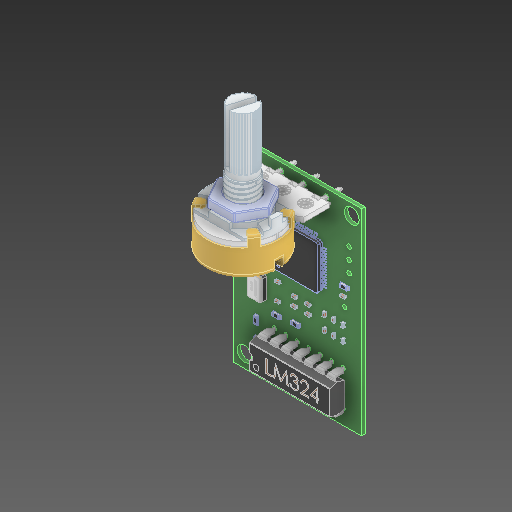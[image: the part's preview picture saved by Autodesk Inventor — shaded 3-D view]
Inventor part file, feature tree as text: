
AUTODESK INVENTOR PART (.ipt)
format: ipt  version: 2020 (Build 240168000, 168)  size: 4,296,704 bytes
history: native  units: in
note: dims shown in document units (in); Inventor stores cm internally (conversion verified against a paired STEP export)
features: other x95, extrude x1
ambient origin geometry x8: Origin, YZ Plane, XZ Plane, XY Plane, X Axis, Y Axis, Z Axis, Center Point
bodies: Solid1 (feature_tree), Solid2 (feature_tree), Solid3 (feature_tree), Solid4 (feature_tree), Solid5 (feature_tree), Solid6 (feature_tree), Solid7 (feature_tree), Solid8 (feature_tree), Solid9 (feature_tree), Solid10 (feature_tree), Solid11 (feature_tree), Solid12 (feature_tree), Solid13 (feature_tree), Solid14 (feature_tree), Solid15 (feature_tree), Solid16 (feature_tree), Solid17 (feature_tree), Solid18 (feature_tree), Solid19 (feature_tree), Solid20 (feature_tree), Solid21 (feature_tree), Solid22 (feature_tree), Solid23 (feature_tree), Solid24 (feature_tree), Solid25 (feature_tree), Solid26 (feature_tree), Solid27 (feature_tree), Solid28 (feature_tree), Solid29 (feature_tree), Solid30 (feature_tree), Solid31 (feature_tree), Solid32 (feature_tree), Solid33 (feature_tree), Solid34 (feature_tree), Solid35 (feature_tree), Solid36 (feature_tree), Solid37 (feature_tree), Solid38 (feature_tree), Solid39 (feature_tree), Solid40 (feature_tree), Solid41 (feature_tree), Solid42 (feature_tree), Solid43 (feature_tree), Solid44 (feature_tree), Solid45 (feature_tree), Solid46 (feature_tree), Solid47 (feature_tree), Solid48 (feature_tree), Solid49 (feature_tree), Solid50 (feature_tree), Solid51 (feature_tree), Solid52 (feature_tree), Solid53 (feature_tree), Solid54 (feature_tree), Solid55 (feature_tree), Solid56 (feature_tree), Solid57 (feature_tree), Solid58 (feature_tree), Solid59 (feature_tree), Solid60 (feature_tree), Solid61 (feature_tree), Solid62 (feature_tree), Solid63 (feature_tree), Solid64 (feature_tree), Solid65 (feature_tree), Solid66 (feature_tree), Solid67 (feature_tree), Solid68 (feature_tree), Solid69 (feature_tree), Solid70 (feature_tree), Solid71 (feature_tree), Solid72 (feature_tree), Solid73 (feature_tree), Solid74 (feature_tree), Solid75 (feature_tree), Solid76 (feature_tree), Solid77 (feature_tree), Solid78 (feature_tree), Solid79 (feature_tree), Solid80 (feature_tree), Solid81 (feature_tree), Solid82 (feature_tree), Solid83 (feature_tree), Solid84 (feature_tree), Solid85 (feature_tree), Solid86 (feature_tree), Solid87 (feature_tree), Solid88 (feature_tree), Solid89 (feature_tree), Solid90 (feature_tree), Solid91 (feature_tree), Solid92 (feature_tree), Solid93 (feature_tree), Solid94 (feature_tree), Solid95 (feature_tree), Solid96 (feature_tree)
feature tree (96):
  other  "Board_718:1"
  other  "Resistencia_719:1"
  other  "Resistencia_721:1"
  other  "Resistencia_723:1"
  other  "Resistencia_725:1"
  other  "Resistencia_727:1"
  other  "lm324_729:1"
  other  "PotentiometerCasing_731:1"
  other  "PotentiometerPCB_732:1"
  other  "PotentiometerShaft_733:1"
  other  "PotentiometerTerminal_734:1"
  other  "PotentiometerTerminal_735:1"
  other  "PotentiometerTerminal_736:1"
  other  "PotentiometerThreadPlate_737:1"
  other  "PotentiometerNut_738:1"
  other  "Crystal_ABM3-16.000MHZ-B2-T_741:1"
  other  "TM4G123C_743:1"
  other  "TM4G123C_743:2"
  other  "TM4G123C_743:3"
  other  "TM4G123C_743:4"
  other  "TM4G123C_743:5"
  other  "TM4G123C_743:6"
  other  "TM4G123C_743:7"
  other  "TM4G123C_743:8"
  other  "TM4G123C_743:9"
  other  "TM4G123C_743:10"
  other  "TM4G123C_743:11"
  other  "TM4G123C_743:12"
  other  "TM4G123C_743:13"
  other  "TM4G123C_743:14"
  other  "TM4G123C_743:15"
  other  "TM4G123C_743:16"
  other  "TM4G123C_743:17"
  other  "TM4G123C_743:18"
  other  "TM4G123C_743:19"
  other  "TM4G123C_743:20"
  other  "TM4G123C_743:21"
  other  "TM4G123C_743:22"
  other  "TM4G123C_743:23"
  other  "TM4G123C_743:24"
  other  "TM4G123C_743:25"
  other  "TM4G123C_743:26"
  other  "TM4G123C_743:27"
  other  "TM4G123C_743:28"
  other  "TM4G123C_743:29"
  other  "TM4G123C_743:30"
  other  "TM4G123C_743:31"
  other  "TM4G123C_743:32"
  other  "TM4G123C_743:33"
  other  "TM4G123C_743:34"
  other  "TM4G123C_743:35"
  other  "TM4G123C_743:36"
  other  "TM4G123C_743:37"
  other  "TM4G123C_743:38"
  other  "TM4G123C_743:39"
  other  "TM4G123C_743:40"
  other  "TM4G123C_743:41"
  other  "TM4G123C_743:42"
  other  "TM4G123C_743:43"
  other  "TM4G123C_743:44"
  other  "TM4G123C_743:45"
  other  "TM4G123C_743:46"
  other  "TM4G123C_743:47"
  other  "TM4G123C_743:48"
  other  "TM4G123C_743:49"
  other  "TM4G123C_743:50"
  other  "TM4G123C_743:51"
  other  "TM4G123C_743:52"
  other  "TM4G123C_743:53"
  other  "TM4G123C_743:54"
  other  "TM4G123C_743:55"
  other  "TM4G123C_743:56"
  other  "TM4G123C_743:57"
  other  "TM4G123C_743:58"
  other  "TM4G123C_743:59"
  other  "TM4G123C_743:60"
  other  "TM4G123C_743:61"
  other  "TM4G123C_743:62"
  other  "TM4G123C_743:63"
  other  "TM4G123C_743:64"
  other  "TM4G123C_743:65"
  extrude  "Extruded_744:1"  [1 undecoded]
  other  "Resistencia_747:1"
  other  "Capacitor_749:1"
  other  "Capacitor_751:1"
  other  "Capacitor_753:1"
  other  "Capacitor_755:1"
  other  "Capacitor_757:1"
  other  "Capacitor_759:1"
  other  "Capacitor_761:1"
  other  "Capacitor_763:1"
  other  "Capacitor_765:1"
  other  "Capacitor_767:1"
  other  "Capacitor_769:1"
  other  "Capacitor_771:1"
  other  "Capacitor_773:1"
note: 1 required parameter value undecoded (feature->parameter linkage not recoverable at this tier; creation-order binding heuristic only, values carry confidence <= 0.55)
